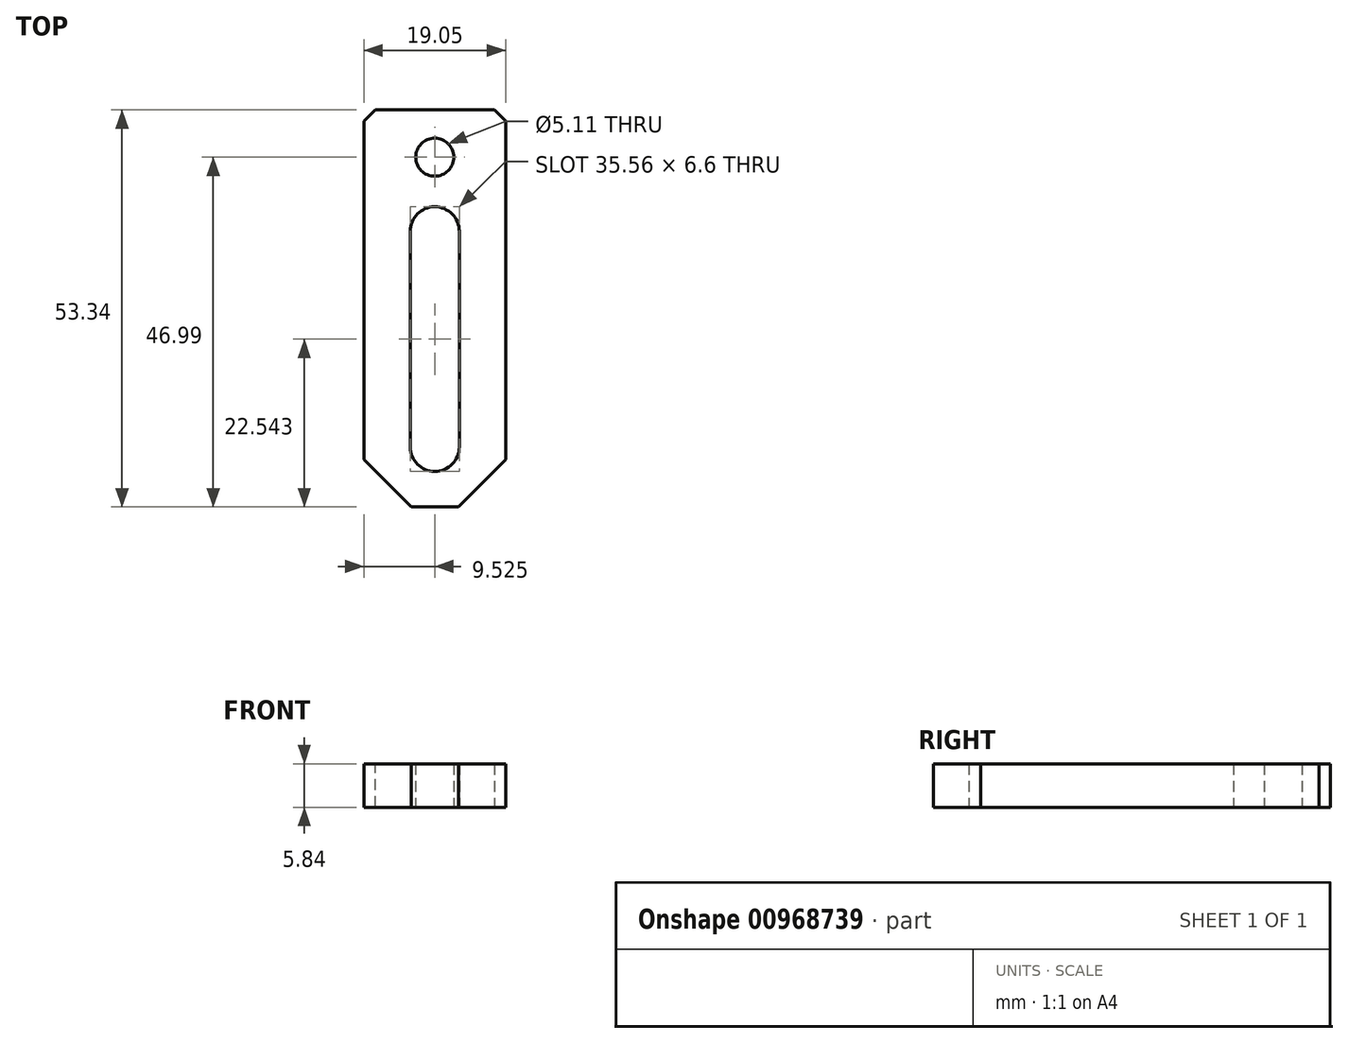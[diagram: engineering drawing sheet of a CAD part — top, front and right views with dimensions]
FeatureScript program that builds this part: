
annotation { "Feature Type Name" : "Feature", "Feature Type Description" : "" }
export const myFeature = defineFeature(function(context is Context, id is Id, definition is map)
    precondition{}
    {
        {
            var Q0;
            Q0=qCreatedBy(makeId("Top.planeOp"),FACE);
            var sketch = newSketch(context, id + "F0", { "sketchPlane" : qUnion([Q0])});
            skLineSegment(sketch, "E0.bottom", {"start": v(0, 0) * mm, "end": v(19.05, 0) * mm});
            skLineSegment(sketch, "E0.top", {"start": v(0, -53.34) * mm, "end": v(19.05, -53.34) * mm});
            skLineSegment(sketch, "E0.left", {"start": v(0, 0) * mm, "end": v(0, -53.34) * mm});
            skLineSegment(sketch, "E0.right", {"start": v(19.05, 0) * mm, "end": v(19.05, -53.34) * mm});
            skLineSegment(sketch, "E1.bottom", {"start": v(9.53, -13.02) * mm, "end": v(9.53, -13.02) * mm});
            skLineSegment(sketch, "E1.top", {"start": v(9.53, -48.58) * mm, "end": v(9.53, -48.58) * mm});
            skLineSegment(sketch, "E1.left", {"start": v(6.22, -16.32) * mm, "end": v(6.22, -45.28) * mm});
            skLineSegment(sketch, "E1.right", {"start": v(12.83, -16.32) * mm, "end": v(12.83, -45.28) * mm});
            skPoint(sketch, "E2.visualSharp", {"position": v(6.22, -13.02) * mm});
            skArc(sketch, "E2.filletArc", {"start": v(9.53, -13.02) * mm, "mid": v(7.2, -13.98) * mm, "end": v(6.22, -16.32) * mm});
            skPoint(sketch, "E3.visualSharp", {"position": v(12.83, -13.02) * mm});
            skArc(sketch, "E3.filletArc", {"start": v(12.83, -16.32) * mm, "mid": v(11.86, -13.98) * mm, "end": v(9.53, -13.02) * mm});
            skPoint(sketch, "E4.visualSharp", {"position": v(6.22, -48.58) * mm});
            skArc(sketch, "E4.filletArc", {"start": v(6.22, -45.28) * mm, "mid": v(7.2, -47.61) * mm, "end": v(9.53, -48.58) * mm});
            skPoint(sketch, "E5.visualSharp", {"position": v(12.83, -48.58) * mm});
            skArc(sketch, "E5.filletArc", {"start": v(9.53, -48.58) * mm, "mid": v(11.86, -47.61) * mm, "end": v(12.83, -45.28) * mm});
            skCircle(sketch, "E6", {"center": v(9.53, -6.35) * mm, "radius": 2.55 * mm});
            skSolve(sketch);
        }
        {
            var Q0;
            Q0=makeQuery(id+"F0.imprint","IMPRINT",FACE,{"disambiguationData":[TD([[makeQuery(id+"F0.imprint","IMPRINT",EDGE,{"derivedFrom":sQuery(id+"F0.wireOp",EDGE,"E0.bottom")}),-1.0]])]});
            extrude(context, id + "F1", {"entities" : qUnion([Q0]), "depth" : 5.84 * mm, "offsetDistance" : 25.4 * mm});
        }
        {
            var Q0;
            Q0=makeQuery(id+"F1.opExtrude","SWEPT_EDGE",EDGE,{"disambiguationData":[OSD([sQuery(id+"F0.wireOp",EDGE,"E0.top"),sQuery(id+"F0.wireOp",EDGE,"E0.left")])]});
            var Q1;
            Q1=makeQuery(id+"F1.opExtrude","SWEPT_EDGE",EDGE,{"disambiguationData":[OSD([sQuery(id+"F0.wireOp",EDGE,"E0.top"),sQuery(id+"F0.wireOp",EDGE,"E0.right")])]});
            chamfer(context, id + "F2", {"entities" : qUnion([Q0, Q1]), "width" : 6.35 * mm, "tangentPropagation" : true});
        }
        {
            var Q0;
            Q0=makeQuery(id+"F1.opExtrude","SWEPT_EDGE",EDGE,{"disambiguationData":[OSD([sQuery(id+"F0.wireOp",EDGE,"E0.bottom"),sQuery(id+"F0.wireOp",EDGE,"E0.right")])]});
            var Q1;
            Q1=makeQuery(id+"F1.opExtrude","SWEPT_EDGE",EDGE,{"disambiguationData":[OSD([sQuery(id+"F0.wireOp",EDGE,"E0.bottom"),sQuery(id+"F0.wireOp",EDGE,"E0.left")])]});
            chamfer(context, id + "F3", {"entities" : qUnion([Q0, Q1]), "width" : 1.52 * mm, "tangentPropagation" : true});
        }
    });
